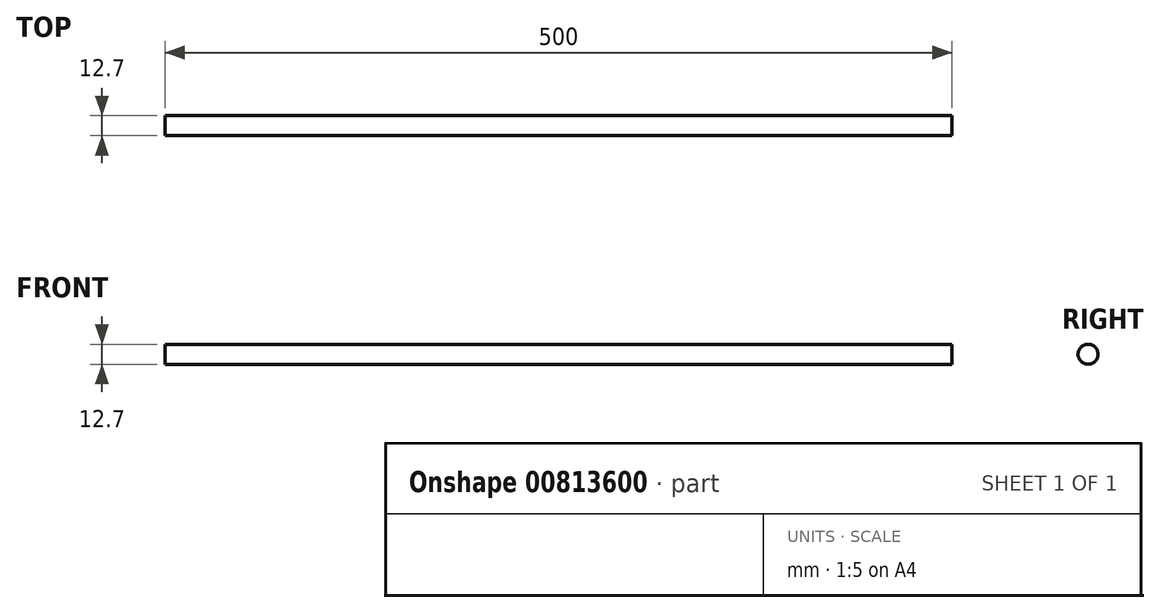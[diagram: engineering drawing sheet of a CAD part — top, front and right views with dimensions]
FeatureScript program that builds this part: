
annotation { "Feature Type Name" : "Feature", "Feature Type Description" : "" }
export const myFeature = defineFeature(function(context is Context, id is Id, definition is map)
    precondition{}
    {
        {
            var Q0;
            Q0=qCreatedBy(makeId("Right.planeOp"),FACE);
            var sketch = newSketch(context, id + "F0", { "sketchPlane" : qUnion([Q0])});
            skCircle(sketch, "E0", {"center": v(0, 0) * mm, "radius": 6.35 * mm});
            skSolve(sketch);
        }
        {
            var Q0;
            Q0=makeQuery(id+"F0.imprint","IMPRINT",FACE,{"disambiguationData":[TD([[makeQuery(id+"F0.imprint","IMPRINT",EDGE,{"derivedFrom":sQuery(id+"F0.wireOp",EDGE,"E0")}),1.0]])]});
            extrude(context, id + "F1", {"entities" : qUnion([Q0]), "depth" : 500 * mm, "offsetDistance" : 25.4 * mm});
        }
    });
